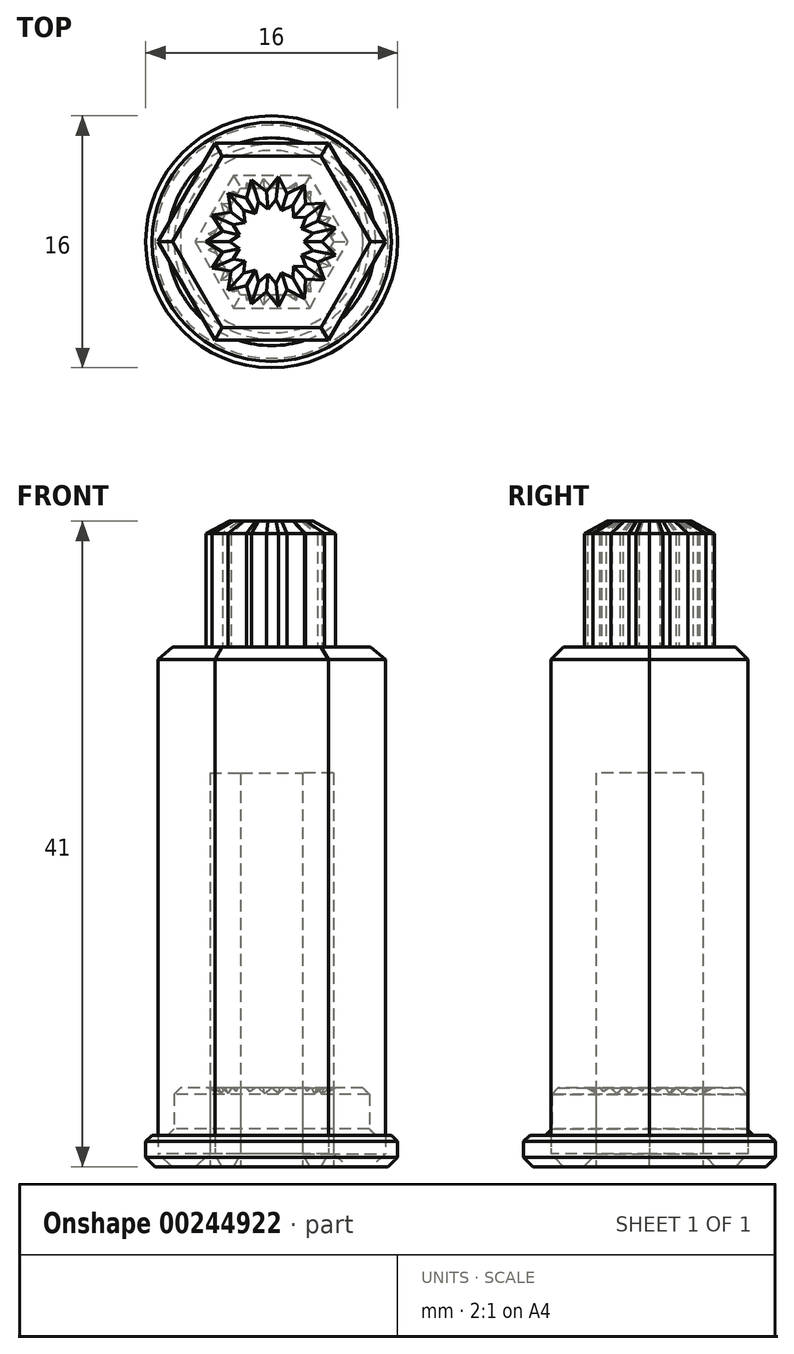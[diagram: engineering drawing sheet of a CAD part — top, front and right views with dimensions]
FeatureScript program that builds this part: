
annotation { "Feature Type Name" : "Feature", "Feature Type Description" : "" }
export const myFeature = defineFeature(function(context is Context, id is Id, definition is map)
    precondition{}
    {
        {
            var Q0;
            Q0=qCreatedBy(makeId("Top.planeOp"),FACE);
            var sketch = newSketch(context, id + "F0", { "sketchPlane" : qUnion([Q0])});
            skCircle(sketch, "E0", {"center": v(0, 0) * mm, "radius": 8 * mm});
            skSolve(sketch);
        }
        {
            var Q0;
            Q0=qSketchRegion(id+"F0",true);
            extrude(context, id + "F1", {"entities" : qUnion([Q0]), "depth" : 2 * mm, "offsetDistance" : 25 * mm});
        }
        {
            var Q0;
            Q0=makeQuery(id+"F1.opExtrude","CAP_FACE",FACE,{"disambiguationData":[OSD([sQuery(id+"F0.wireOp",EDGE,"ZvkXPhkh-jxfF-Gfea-dxrh-XISQfD8u4X7v"),sQuery(id+"F0.wireOp",EDGE,"E0")])],"isStart":false});
            var sketch = newSketch(context, id + "F2", { "sketchPlane" : qUnion([Q0])});
            skCircle(sketch, "E1", {"center": v(11, 0) * mm, "radius": 1 * mm});
            skCircle(sketch, "E2.1.0", {"center": v(0, 11) * mm, "radius": 1 * mm});
            skCircle(sketch, "E2.2.0", {"center": v(-11, 0) * mm, "radius": 1 * mm});
            skCircle(sketch, "E2.3.0", {"center": v(0, -11) * mm, "radius": 1 * mm});
            skPoint(sketch, "E2.center", {"position": v(0, 0) * mm});
            skCircle(sketch, "E3", {"center": v(16, 0) * mm, "radius": 1.6 * mm});
            skCircle(sketch, "E4.1.0", {"center": v(0, 16) * mm, "radius": 1.6 * mm});
            skCircle(sketch, "E4.2.0", {"center": v(-16, 0) * mm, "radius": 1.6 * mm});
            skCircle(sketch, "E4.3.0", {"center": v(0, -16) * mm, "radius": 1.6 * mm});
            skLineSegment(sketch, "E5", {"start": v(0, 0) * mm, "end": v(7.78, 7.78) * mm});
            skLineSegment(sketch, "E6", {"start": v(7.78, 7.78) * mm, "end": v(11.1, 11.1) * mm});
            skCircle(sketch, "E7", {"center": v(7.78, 7.78) * mm, "radius": 1.6 * mm});
            skCircle(sketch, "E8", {"center": v(11.1, 11.1) * mm, "radius": 1 * mm});
            skCircle(sketch, "E9.1.0", {"center": v(-7.78, 7.78) * mm, "radius": 1.6 * mm});
            skCircle(sketch, "E9.1.1", {"center": v(-11.1, 11.1) * mm, "radius": 1 * mm});
            skCircle(sketch, "E9.2.0", {"center": v(-7.78, -7.78) * mm, "radius": 1.6 * mm});
            skCircle(sketch, "E9.2.1", {"center": v(-11.1, -11.1) * mm, "radius": 1 * mm});
            skCircle(sketch, "E9.3.0", {"center": v(7.78, -7.78) * mm, "radius": 1.6 * mm});
            skCircle(sketch, "E9.3.1", {"center": v(11.1, -11.1) * mm, "radius": 1 * mm});
            skSolve(sketch);
        }
        {
            var Q0;
            Q0=qSketchRegion(id+"F2",true);
            extrude(context, id + "F3", {"entities" : qUnion([Q0]), "operationType" : NewBodyOperationType.REMOVE, "oppositeDirection" : true, "depth" : 10 * mm, "offsetDistance" : 25 * mm});
        }
        {
            var Q0;
            Q0=makeQuery(id+"F1.opExtrude","CAP_FACE",FACE,{"disambiguationData":[OSD([sQuery(id+"F0.wireOp",EDGE,"E0")])],"isStart":false});
            var sketch = newSketch(context, id + "F4", { "sketchPlane" : qUnion([Q0])});
            skCircle(sketch, "E10", {"center": v(0, 0) * mm, "radius": 6.2 * mm});
            skSolve(sketch);
        }
        {
            var Q0;
            Q0=qSketchRegion(id+"F4",true);
            extrude(context, id + "F5", {"entities" : qUnion([Q0]), "operationType" : NewBodyOperationType.ADD, "depth" : 3 * mm, "offsetDistance" : 25 * mm});
        }
        {
            var Q0;
            Q0=makeQuery(id+"F5.opExtrude","CAP_FACE",FACE,{"disambiguationData":[OSD([sQuery(id+"F4.wireOp",EDGE,"E10")])],"isStart":false});
            var sketch = newSketch(context, id + "F6", { "sketchPlane" : qUnion([Q0])});
            skLineSegment(sketch, "E11", {"start": v(2.8, 0) * mm, "end": v(3.3, 0.43) * mm});
            skLineSegment(sketch, "E12.MirrorCS", {"start": v(2.8, 0) * mm, "end": v(3.3, -0.43) * mm});
            skLineSegment(sketch, "E13.1.0", {"start": v(2.7, 0.72) * mm, "end": v(3.08, 1.27) * mm});
            skLineSegment(sketch, "E13.1.1", {"start": v(2.7, 0.72) * mm, "end": v(3.3, 0.43) * mm});
            skLineSegment(sketch, "E13.2.0", {"start": v(2.42, 1.4) * mm, "end": v(2.64, 2.03) * mm});
            skLineSegment(sketch, "E13.2.1", {"start": v(2.42, 1.4) * mm, "end": v(3.08, 1.27) * mm});
            skLineSegment(sketch, "E13.3.0", {"start": v(1.98, 1.98) * mm, "end": v(2.03, 2.64) * mm});
            skLineSegment(sketch, "E13.3.1", {"start": v(1.98, 1.98) * mm, "end": v(2.64, 2.03) * mm});
            skLineSegment(sketch, "E13.4.0", {"start": v(1.4, 2.42) * mm, "end": v(1.27, 3.08) * mm});
            skLineSegment(sketch, "E13.4.1", {"start": v(1.4, 2.42) * mm, "end": v(2.03, 2.64) * mm});
            skLineSegment(sketch, "E13.5.0", {"start": v(0.72, 2.7) * mm, "end": v(0.43, 3.3) * mm});
            skLineSegment(sketch, "E13.5.1", {"start": v(0.72, 2.7) * mm, "end": v(1.27, 3.08) * mm});
            skLineSegment(sketch, "E13.6.0", {"start": v(0, 2.8) * mm, "end": v(-0.43, 3.3) * mm});
            skLineSegment(sketch, "E13.6.1", {"start": v(0, 2.8) * mm, "end": v(0.43, 3.3) * mm});
            skLineSegment(sketch, "E13.7.0", {"start": v(-0.72, 2.7) * mm, "end": v(-1.27, 3.08) * mm});
            skLineSegment(sketch, "E13.7.1", {"start": v(-0.72, 2.7) * mm, "end": v(-0.43, 3.3) * mm});
            skLineSegment(sketch, "E13.8.0", {"start": v(-1.4, 2.42) * mm, "end": v(-2.03, 2.64) * mm});
            skLineSegment(sketch, "E13.8.1", {"start": v(-1.4, 2.42) * mm, "end": v(-1.27, 3.08) * mm});
            skLineSegment(sketch, "E13.9.0", {"start": v(-1.98, 1.98) * mm, "end": v(-2.64, 2.03) * mm});
            skLineSegment(sketch, "E13.9.1", {"start": v(-1.98, 1.98) * mm, "end": v(-2.03, 2.64) * mm});
            skLineSegment(sketch, "E13.10.0", {"start": v(-2.42, 1.4) * mm, "end": v(-3.08, 1.27) * mm});
            skLineSegment(sketch, "E13.10.1", {"start": v(-2.42, 1.4) * mm, "end": v(-2.64, 2.03) * mm});
            skLineSegment(sketch, "E13.11.0", {"start": v(-2.7, 0.72) * mm, "end": v(-3.3, 0.43) * mm});
            skLineSegment(sketch, "E13.11.1", {"start": v(-2.7, 0.72) * mm, "end": v(-3.08, 1.27) * mm});
            skLineSegment(sketch, "E13.12.0", {"start": v(-2.8, 0) * mm, "end": v(-3.3, -0.43) * mm});
            skLineSegment(sketch, "E13.12.1", {"start": v(-2.8, 0) * mm, "end": v(-3.3, 0.43) * mm});
            skLineSegment(sketch, "E13.13.0", {"start": v(-2.7, -0.72) * mm, "end": v(-3.08, -1.27) * mm});
            skLineSegment(sketch, "E13.13.1", {"start": v(-2.7, -0.72) * mm, "end": v(-3.3, -0.43) * mm});
            skLineSegment(sketch, "E13.14.0", {"start": v(-2.42, -1.4) * mm, "end": v(-2.64, -2.03) * mm});
            skLineSegment(sketch, "E13.14.1", {"start": v(-2.42, -1.4) * mm, "end": v(-3.08, -1.27) * mm});
            skPoint(sketch, "E13.center", {"position": v(0, 0) * mm});
            skLineSegment(sketch, "E14.1.15.0", {"start": v(-1.98, -1.98) * mm, "end": v(-2.03, -2.64) * mm});
            skLineSegment(sketch, "E14.3.15.0", {"start": v(-1.98, -1.98) * mm, "end": v(-2.64, -2.03) * mm});
            skLineSegment(sketch, "E14.1.16.0", {"start": v(-1.4, -2.42) * mm, "end": v(-1.27, -3.08) * mm});
            skLineSegment(sketch, "E14.3.16.0", {"start": v(-1.4, -2.42) * mm, "end": v(-2.03, -2.64) * mm});
            skLineSegment(sketch, "E14.1.17.0", {"start": v(-0.72, -2.7) * mm, "end": v(-0.43, -3.3) * mm});
            skLineSegment(sketch, "E14.3.17.0", {"start": v(-0.72, -2.7) * mm, "end": v(-1.27, -3.08) * mm});
            skLineSegment(sketch, "E14.1.18.0", {"start": v(0, -2.8) * mm, "end": v(0.43, -3.3) * mm});
            skLineSegment(sketch, "E14.3.18.0", {"start": v(0, -2.8) * mm, "end": v(-0.43, -3.3) * mm});
            skLineSegment(sketch, "E14.1.19.0", {"start": v(0.72, -2.7) * mm, "end": v(1.27, -3.08) * mm});
            skLineSegment(sketch, "E14.3.19.0", {"start": v(0.72, -2.7) * mm, "end": v(0.43, -3.3) * mm});
            skLineSegment(sketch, "E14.1.20.0", {"start": v(1.4, -2.42) * mm, "end": v(2.03, -2.64) * mm});
            skLineSegment(sketch, "E14.3.20.0", {"start": v(1.4, -2.42) * mm, "end": v(1.27, -3.08) * mm});
            skLineSegment(sketch, "E14.1.21.0", {"start": v(1.98, -1.98) * mm, "end": v(2.64, -2.03) * mm});
            skLineSegment(sketch, "E14.3.21.0", {"start": v(1.98, -1.98) * mm, "end": v(2.03, -2.64) * mm});
            skLineSegment(sketch, "E14.1.22.0", {"start": v(2.42, -1.4) * mm, "end": v(3.08, -1.27) * mm});
            skLineSegment(sketch, "E14.3.22.0", {"start": v(2.42, -1.4) * mm, "end": v(2.64, -2.03) * mm});
            skLineSegment(sketch, "E14.1.23.0", {"start": v(2.7, -0.72) * mm, "end": v(3.3, -0.43) * mm});
            skLineSegment(sketch, "E14.3.23.0", {"start": v(2.7, -0.72) * mm, "end": v(3.08, -1.27) * mm});
            skSolve(sketch);
        }
        {
            var Q0;
            Q0=qSketchRegion(id+"F6",true);
            extrude(context, id + "F7", {"entities" : qUnion([Q0]), "operationType" : NewBodyOperationType.REMOVE, "oppositeDirection" : true, "depth" : 25 * mm, "offsetDistance" : 25 * mm});
        }
        {
            var Q0;
            Q0=qCreatedBy(makeId("Top.planeOp"),FACE);
            var sketch = newSketch(context, id + "F8", { "sketchPlane" : qUnion([Q0])});
            skCircle(sketch, "E15", {"center": v(0, 0) * mm, "radius": 6 * mm});
            skCircle(sketch, "E16", {"center": v(0, 0) * mm, "radius": 1.8 * mm});
            skSolve(sketch);
        }
        {
            var Q0;
            Q0=qSketchRegion(id+"F8",true);
            extrude(context, id + "F9", {"entities" : qUnion([Q0]), "operationType" : NewBodyOperationType.ADD, "depth" : 2 * mm, "offsetDistance" : 25 * mm});
        }
        {
            var Q0;
            Q0=makeQuery(id+"F1.opExtrude","CAP_FACE",FACE,{"disambiguationData":[OSD([sQuery(id+"F0.wireOp",EDGE,"E0")])],"isStart":true});
            chamfer(context, id + "F10", {"entities" : qUnion([Q0]), "width" : .6 * mm, "tangentPropagation" : true});
        }
        {
            var Q0;
            Q0=makeQuery(id+"F5.opExtrude","CAP_FACE",FACE,{"disambiguationData":[OSD([sQuery(id+"F4.wireOp",EDGE,"E10")])],"isStart":false});
            var Q1;
            Q1=makeQuery(id+"F1.opExtrude","CAP_FACE",FACE,{"disambiguationData":[OSD([sQuery(id+"F0.wireOp",EDGE,"E0")])],"isStart":false});
            chamfer(context, id + "F11", {"entities" : qUnion([Q0, Q1]), "width" : .4 * mm, "tangentPropagation" : true});
        }
        {
            var Q0;
            Q0=qCreatedBy(makeId("Top.planeOp"),FACE);
            var sketch = newSketch(context, id + "F12", { "sketchPlane" : qUnion([Q0])});
            skCircle(sketch, "E17.cCircle", {"center": v(0, 0) * mm, "radius": 6.25 * mm, "construction": true});
            skLineSegment(sketch, "E17.0", {"start": v(-3.6, 6.25) * mm, "end": v(3.6, 6.25) * mm});
            skLineSegment(sketch, "E17.1", {"start": v(3.6, 6.25) * mm, "end": v(7.22, 0) * mm});
            skLineSegment(sketch, "E17.2", {"start": v(7.22, 0) * mm, "end": v(3.6, -6.25) * mm});
            skLineSegment(sketch, "E17.3", {"start": v(3.6, -6.25) * mm, "end": v(-3.6, -6.25) * mm});
            skLineSegment(sketch, "E17.4", {"start": v(-3.6, -6.25) * mm, "end": v(-7.22, 0) * mm});
            skLineSegment(sketch, "E17.5", {"start": v(-7.22, 0) * mm, "end": v(-3.6, 6.25) * mm});
            skPoint(sketch, "E17.0.midPoint", {"position": v(0, 6.25) * mm});
            skSolve(sketch);
        }
        {
            var Q0;
            Q0=qSketchRegion(id+"F12",true);
            extrude(context, id + "F13", {"entities" : qUnion([Q0]), "depth" : 30 * mm, "offsetDistance" : 25 * mm});
        }
        {
            var Q0;
            Q0=makeQuery(id+"F13.opExtrude","CAP_FACE",FACE,{"disambiguationData":[OSD([sQuery(id+"F12.wireOp",EDGE,"E17.0"),sQuery(id+"F12.wireOp",EDGE,"E17.1"),sQuery(id+"F12.wireOp",EDGE,"E17.2"),sQuery(id+"F12.wireOp",EDGE,"E17.3"),sQuery(id+"F12.wireOp",EDGE,"E17.4"),sQuery(id+"F12.wireOp",EDGE,"E17.5")])],"isStart":true});
            var sketch = newSketch(context, id + "F14", { "sketchPlane" : qUnion([Q0])});
            skCircle(sketch, "E18.cCircle", {"center": v(0, 0) * mm, "radius": 3.4 * mm, "construction": true});
            skLineSegment(sketch, "E18.0", {"start": v(-1.96, 3.4) * mm, "end": v(1.96, 3.4) * mm});
            skLineSegment(sketch, "E18.1", {"start": v(1.96, 3.4) * mm, "end": v(3.93, 0) * mm});
            skLineSegment(sketch, "E18.2", {"start": v(3.93, 0) * mm, "end": v(1.96, -3.4) * mm});
            skLineSegment(sketch, "E18.3", {"start": v(1.96, -3.4) * mm, "end": v(-1.96, -3.4) * mm});
            skLineSegment(sketch, "E18.4", {"start": v(-1.96, -3.4) * mm, "end": v(-3.93, 0) * mm});
            skLineSegment(sketch, "E18.5", {"start": v(-3.93, 0) * mm, "end": v(-1.96, 3.4) * mm});
            skPoint(sketch, "E18.0.midPoint", {"position": v(0, 3.4) * mm});
            skSolve(sketch);
        }
        {
            var Q0;
            Q0=qSketchRegion(id+"F14",true);
            extrude(context, id + "F15", {"entities" : qUnion([Q0]), "operationType" : NewBodyOperationType.REMOVE, "oppositeDirection" : true, "depth" : 25 * mm, "offsetDistance" : 25 * mm});
        }
        {
            var Q0;
            Q0=makeQuery(id+"F13.opExtrude","CAP_FACE",FACE,{"disambiguationData":[OSD([sQuery(id+"F12.wireOp",EDGE,"E17.0"),sQuery(id+"F12.wireOp",EDGE,"E17.1"),sQuery(id+"F12.wireOp",EDGE,"E17.2"),sQuery(id+"F12.wireOp",EDGE,"E17.3"),sQuery(id+"F12.wireOp",EDGE,"E17.4"),sQuery(id+"F12.wireOp",EDGE,"E17.5")])],"isStart":false});
            var sketch = newSketch(context, id + "F16", { "sketchPlane" : qUnion([Q0])});
            skCircle(sketch, "E19.cCircle", {"center": v(0, 0) * mm, "radius": 6.25 * mm, "construction": true});
            skLineSegment(sketch, "E19.0", {"start": v(-3.6, 6.25) * mm, "end": v(3.6, 6.25) * mm});
            skLineSegment(sketch, "E19.1", {"start": v(3.6, 6.25) * mm, "end": v(7.22, 0) * mm});
            skLineSegment(sketch, "E19.2", {"start": v(7.22, 0) * mm, "end": v(3.6, -6.25) * mm});
            skLineSegment(sketch, "E19.3", {"start": v(3.6, -6.25) * mm, "end": v(-3.6, -6.25) * mm});
            skLineSegment(sketch, "E19.4", {"start": v(-3.6, -6.25) * mm, "end": v(-7.22, 0) * mm});
            skLineSegment(sketch, "E19.5", {"start": v(-7.22, 0) * mm, "end": v(-3.6, 6.25) * mm});
            skPoint(sketch, "E19.0.midPoint", {"position": v(0, 6.25) * mm});
            skSolve(sketch);
        }
        {
            var Q0;
            Q0=qSketchRegion(id+"F16",true);
            extrude(context, id + "F17", {"entities" : qUnion([Q0]), "operationType" : NewBodyOperationType.ADD, "depth" : 3 * mm, "offsetDistance" : 25 * mm});
        }
        {
            var Q0;
            Q0=makeQuery(id+"F17.opExtrude","CAP_FACE",FACE,{"disambiguationData":[OSD([sQuery(id+"F16.wireOp",EDGE,"E19.0"),sQuery(id+"F16.wireOp",EDGE,"E19.1"),sQuery(id+"F16.wireOp",EDGE,"E19.2"),sQuery(id+"F16.wireOp",EDGE,"E19.3"),sQuery(id+"F16.wireOp",EDGE,"E19.4"),sQuery(id+"F16.wireOp",EDGE,"E19.5")])],"isStart":false});
            var Q1;
            Q1=makeQuery(id+"F13.opExtrude","CAP_FACE",FACE,{"disambiguationData":[OSD([sQuery(id+"F12.wireOp",EDGE,"E17.0"),sQuery(id+"F12.wireOp",EDGE,"E17.1"),sQuery(id+"F12.wireOp",EDGE,"E17.2"),sQuery(id+"F12.wireOp",EDGE,"E17.3"),sQuery(id+"F12.wireOp",EDGE,"E17.4"),sQuery(id+"F12.wireOp",EDGE,"E17.5")])],"isStart":true});
            chamfer(context, id + "F18", {"entities" : qUnion([Q0, Q1]), "width" : .8 * mm, "tangentPropagation" : true});
        }
        {
            var Q0;
            Q0=makeQuery(id+"F17.opExtrude","CAP_FACE",FACE,{"disambiguationData":[OSD([sQuery(id+"F16.wireOp",EDGE,"E19.0"),sQuery(id+"F16.wireOp",EDGE,"E19.1"),sQuery(id+"F16.wireOp",EDGE,"E19.2"),sQuery(id+"F16.wireOp",EDGE,"E19.3"),sQuery(id+"F16.wireOp",EDGE,"E19.4"),sQuery(id+"F16.wireOp",EDGE,"E19.5")])],"isStart":false});
            var sketch = newSketch(context, id + "F19", { "sketchPlane" : qUnion([Q0])});
            skLineSegment(sketch, "E20", {"start": v(3.2, 0) * mm, "end": v(4.1, 0.9) * mm});
            skLineSegment(sketch, "E21.MirrorCS", {"start": v(3.2, 0) * mm, "end": v(4.1, -0.9) * mm});
            skLineSegment(sketch, "E22.1.0", {"start": v(2.92, 1.3) * mm, "end": v(4.11, 0.85) * mm});
            skLineSegment(sketch, "E22.1.1", {"start": v(2.92, 1.3) * mm, "end": v(3.38, 2.49) * mm});
            skLineSegment(sketch, "E22.2.0", {"start": v(2.14, 2.38) * mm, "end": v(3.41, 2.44) * mm});
            skLineSegment(sketch, "E22.2.1", {"start": v(2.14, 2.38) * mm, "end": v(2.07, 3.65) * mm});
            skLineSegment(sketch, "E22.3.0", {"start": v(0.99, 3.04) * mm, "end": v(2.12, 3.62) * mm});
            skLineSegment(sketch, "E22.3.1", {"start": v(0.99, 3.04) * mm, "end": v(0.41, 4.18) * mm});
            skLineSegment(sketch, "E22.4.0", {"start": v(-0.33, 3.18) * mm, "end": v(0.47, 4.17) * mm});
            skLineSegment(sketch, "E22.4.1", {"start": v(-0.33, 3.18) * mm, "end": v(-1.32, 3.98) * mm});
            skLineSegment(sketch, "E22.5.0", {"start": v(-1.6, 2.77) * mm, "end": v(-1.27, 4) * mm});
            skLineSegment(sketch, "E22.5.1", {"start": v(-1.6, 2.77) * mm, "end": v(-2.83, 3.1) * mm});
            skLineSegment(sketch, "E22.6.0", {"start": v(-2.59, 1.88) * mm, "end": v(-2.79, 3.14) * mm});
            skLineSegment(sketch, "E22.6.1", {"start": v(-2.59, 1.88) * mm, "end": v(-3.85, 1.68) * mm});
            skLineSegment(sketch, "E22.7.0", {"start": v(-3.13, 0.67) * mm, "end": v(-3.82, 1.73) * mm});
            skLineSegment(sketch, "E22.7.1", {"start": v(-3.13, 0.67) * mm, "end": v(-4.2, -0.03) * mm});
            skLineSegment(sketch, "E22.8.0", {"start": v(-3.13, -0.67) * mm, "end": v(-4.2, 0.03) * mm});
            skLineSegment(sketch, "E22.8.1", {"start": v(-3.13, -0.67) * mm, "end": v(-3.82, -1.73) * mm});
            skLineSegment(sketch, "E22.9.0", {"start": v(-2.59, -1.88) * mm, "end": v(-3.85, -1.68) * mm});
            skLineSegment(sketch, "E22.9.1", {"start": v(-2.59, -1.88) * mm, "end": v(-2.79, -3.14) * mm});
            skLineSegment(sketch, "E22.10.0", {"start": v(-1.6, -2.77) * mm, "end": v(-2.83, -3.1) * mm});
            skLineSegment(sketch, "E22.10.1", {"start": v(-1.6, -2.77) * mm, "end": v(-1.27, -4) * mm});
            skLineSegment(sketch, "E22.11.0", {"start": v(-0.33, -3.18) * mm, "end": v(-1.32, -3.98) * mm});
            skLineSegment(sketch, "E22.11.1", {"start": v(-0.33, -3.18) * mm, "end": v(0.47, -4.17) * mm});
            skLineSegment(sketch, "E22.12.0", {"start": v(0.99, -3.04) * mm, "end": v(0.41, -4.18) * mm});
            skLineSegment(sketch, "E22.12.1", {"start": v(0.99, -3.04) * mm, "end": v(2.12, -3.62) * mm});
            skLineSegment(sketch, "E22.13.0", {"start": v(2.14, -2.38) * mm, "end": v(2.07, -3.65) * mm});
            skLineSegment(sketch, "E22.13.1", {"start": v(2.14, -2.38) * mm, "end": v(3.41, -2.44) * mm});
            skLineSegment(sketch, "E22.14.0", {"start": v(2.92, -1.3) * mm, "end": v(3.38, -2.49) * mm});
            skLineSegment(sketch, "E22.14.1", {"start": v(2.92, -1.3) * mm, "end": v(4.11, -0.85) * mm});
            skPoint(sketch, "E22.center", {"position": v(0, 0) * mm});
            skSolve(sketch);
        }
        {
            var Q0;
            Q0=qSketchRegion(id+"F19",true);
            extrude(context, id + "F20", {"entities" : qUnion([Q0]), "operationType" : NewBodyOperationType.ADD, "depth" : 8 * mm, "offsetDistance" : 25 * mm});
        }
        {
            var Q0;
            Q0=makeQuery(id+"F13.opExtrude","CAP_FACE",FACE,{"disambiguationData":[OSD([sQuery(id+"F12.wireOp",EDGE,"N6ndEIrb-N8uo-6AdX-TBZU-aG1VvkIupD5g")])],"isStart":true});
            var Q1;
            Q1=makeQuery(id+"F20.opExtrude","CAP_FACE",FACE,{"disambiguationData":[OSD([sQuery(id+"F19.wireOp",EDGE,"E20"),sQuery(id+"F19.wireOp",EDGE,"E21.MirrorCS"),sQuery(id+"F19.wireOp",EDGE,"E22.1.0"),sQuery(id+"F19.wireOp",EDGE,"E22.1.1"),sQuery(id+"F19.wireOp",EDGE,"E22.2.0"),sQuery(id+"F19.wireOp",EDGE,"E22.2.1"),sQuery(id+"F19.wireOp",EDGE,"E22.3.0"),sQuery(id+"F19.wireOp",EDGE,"E22.3.1"),sQuery(id+"F19.wireOp",EDGE,"E22.4.0"),sQuery(id+"F19.wireOp",EDGE,"E22.4.1"),sQuery(id+"F19.wireOp",EDGE,"E22.5.0"),sQuery(id+"F19.wireOp",EDGE,"E22.5.1"),sQuery(id+"F19.wireOp",EDGE,"E22.6.0"),sQuery(id+"F19.wireOp",EDGE,"E22.6.1"),sQuery(id+"F19.wireOp",EDGE,"E22.7.0"),sQuery(id+"F19.wireOp",EDGE,"E22.7.1"),sQuery(id+"F19.wireOp",EDGE,"E22.8.0"),sQuery(id+"F19.wireOp",EDGE,"E22.8.1"),sQuery(id+"F19.wireOp",EDGE,"E22.9.0"),sQuery(id+"F19.wireOp",EDGE,"E22.9.1"),sQuery(id+"F19.wireOp",EDGE,"E22.10.0"),sQuery(id+"F19.wireOp",EDGE,"E22.10.1"),sQuery(id+"F19.wireOp",EDGE,"E22.11.0"),sQuery(id+"F19.wireOp",EDGE,"E22.11.1"),sQuery(id+"F19.wireOp",EDGE,"E22.12.0"),sQuery(id+"F19.wireOp",EDGE,"E22.12.1"),sQuery(id+"F19.wireOp",EDGE,"E22.13.0"),sQuery(id+"F19.wireOp",EDGE,"E22.13.1"),sQuery(id+"F19.wireOp",EDGE,"E22.14.0"),sQuery(id+"F19.wireOp",EDGE,"E22.14.1")])],"isStart":false});
            chamfer(context, id + "F21", {"entities" : qUnion([Q0, Q1]), "width" : .8 * mm, "tangentPropagation" : true});
        }
    });
